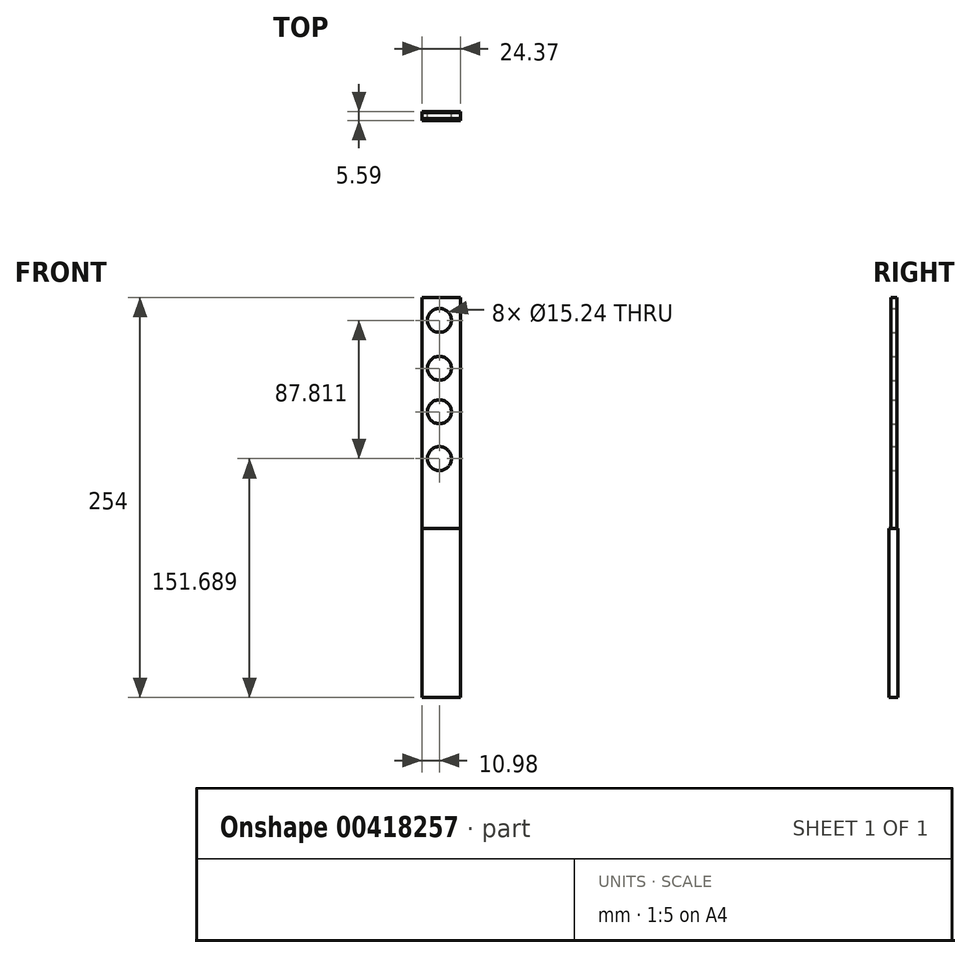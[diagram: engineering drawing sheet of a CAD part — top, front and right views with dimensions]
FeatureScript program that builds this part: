
annotation { "Feature Type Name" : "Feature", "Feature Type Description" : "" }
export const myFeature = defineFeature(function(context is Context, id is Id, definition is map)
    precondition{}
    {
        {
            var Q0;
            Q0=qCreatedBy(makeId("Front.planeOp"),FACE);
            var sketch = newSketch(context, id + "F0", { "sketchPlane" : qUnion([Q0])});
            skLineSegment(sketch, "E0.bottom", {"start": v(-13.96, 126.44) * mm, "end": v(10.4, 126.44) * mm});
            skLineSegment(sketch, "E0.top", {"start": v(-13.96, -127.56) * mm, "end": v(10.4, -127.56) * mm});
            skLineSegment(sketch, "E0.left", {"start": v(-13.96, 126.44) * mm, "end": v(-13.96, -127.56) * mm});
            skLineSegment(sketch, "E0.right", {"start": v(10.4, 126.44) * mm, "end": v(10.4, -127.56) * mm});
            skCircle(sketch, "E1", {"center": v(-2.98, 111.94) * mm, "radius": 7.62 * mm});
            skCircle(sketch, "E2", {"center": v(-2.98, 81.5) * mm, "radius": 7.62 * mm});
            skCircle(sketch, "E3", {"center": v(-2.98, 53.86) * mm, "radius": 7.62 * mm});
            skCircle(sketch, "E4", {"center": v(-2.98, 24.13) * mm, "radius": 7.62 * mm});
            skLineSegment(sketch, "E5", {"start": v(-13.96, -20.25) * mm, "end": v(10.4, -20.25) * mm});
            skSolve(sketch);
        }
        {
            var Q0;
            {var subQ1=sQuery(id+"F0.wireOp",EDGE,"E0.bottom");Q0=makeQuery(id+"F0.imprint","IMPRINT",FACE,{"disambiguationData":[TD([[makeQuery(id+"F0.imprint","IMPRINT",EDGE,{"derivedFrom":subQ1}),-1.0]])]});}
            extrude(context, id + "F1", {"entities" : qUnion([Q0]), "depth" : 3.8 * mm});
        }
        {
            var Q0;
            {var subQ0=sQuery(id+"F0.wireOp",EDGE,"E0.top");Q0=makeQuery(id+"F0.imprint","IMPRINT",FACE,{"disambiguationData":[TD([[makeQuery(id+"F0.imprint","IMPRINT",EDGE,{"derivedFrom":subQ0}),1.0]])]});}
            extrude(context, id + "F2", {"entities" : qUnion([Q0]), "depth" : 5.08 * mm, "hasSecondDirection" : true, "secondDirectionOppositeDirection" : true, "secondDirectionDepth" : 0.5 * mm});
        }
    });
